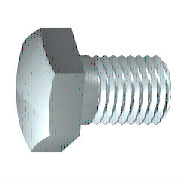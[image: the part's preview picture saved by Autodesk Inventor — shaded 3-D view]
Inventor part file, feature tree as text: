
AUTODESK INVENTOR PART (.ipt)
format: ipt  version: 2020 (Build 240168000, 168)  size: 197,120 bytes
history: native  units: mm (DEFAULTED — no unit token found)
features: sketch x3, extrude x1, chamfer x1, plane x1
ambient origin geometry x7: Origin, YZ Plane, XZ Plane, X Axis, Y Axis, Z Axis, Center Point
bodies: Solid1 (feature_tree), Body (feature_tree)
feature tree (6):
  extrude  "Head"  Depth=17.9mm
  chamfer  "Chamfer1"  Distance=2.4mm
  plane  "Work Plane1"
  sketch  "Sketch1"  dims[d0=20.0mm d1=17.9mm]
  sketch  "Sketch2"  dims[d2=4.0mm]
  sketch  "Sketch4"  dims[d12=90.0deg d3=2.4mm d4=0.0mm d5=30.0deg d21=90.0deg d6=0.429415mm d7=0.429515mm d8=0.0mm d9=0.4001mm d10=5.9mm d11=7.0mm d13=0.429515mm d14=3.621114mm d15=17.9mm d16=0.0mm d19=7.0mm d55=45.0deg d57=0.0mm d58=0.0mm]
